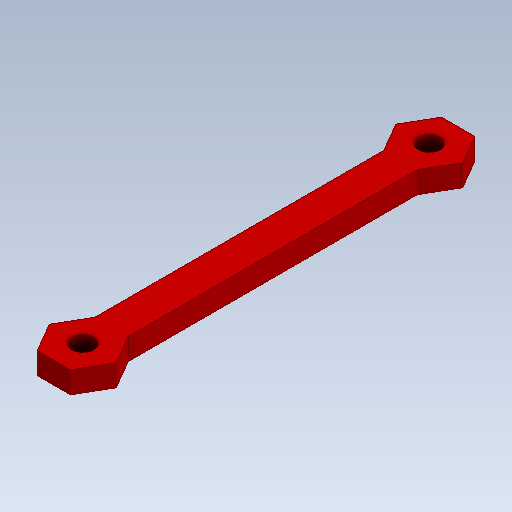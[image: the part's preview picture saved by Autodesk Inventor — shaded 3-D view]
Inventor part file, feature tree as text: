
AUTODESK INVENTOR PART (.ipt)
format: ipt  version: 2020 (Build 240168000, 168)  size: 115,712 bytes
history: native  units: in
note: dims shown in document units (in); Inventor stores cm internally (conversion verified against a paired STEP export)
features: extrude x1, sketch x1
ambient origin geometry x8: Origin, YZ Plane, XZ Plane, XY Plane, X Axis, Y Axis, Z Axis, Center Point
bodies: Solid1 (feature_tree)
feature tree (2):
  extrude  "Extrusion1"  Depth=0.315in
  sketch  "Sketch1"  dims[d1=1.5748in d2=0.315in d3=0.122in d4=0.122in d5=0.1181in d6=0.0in]
